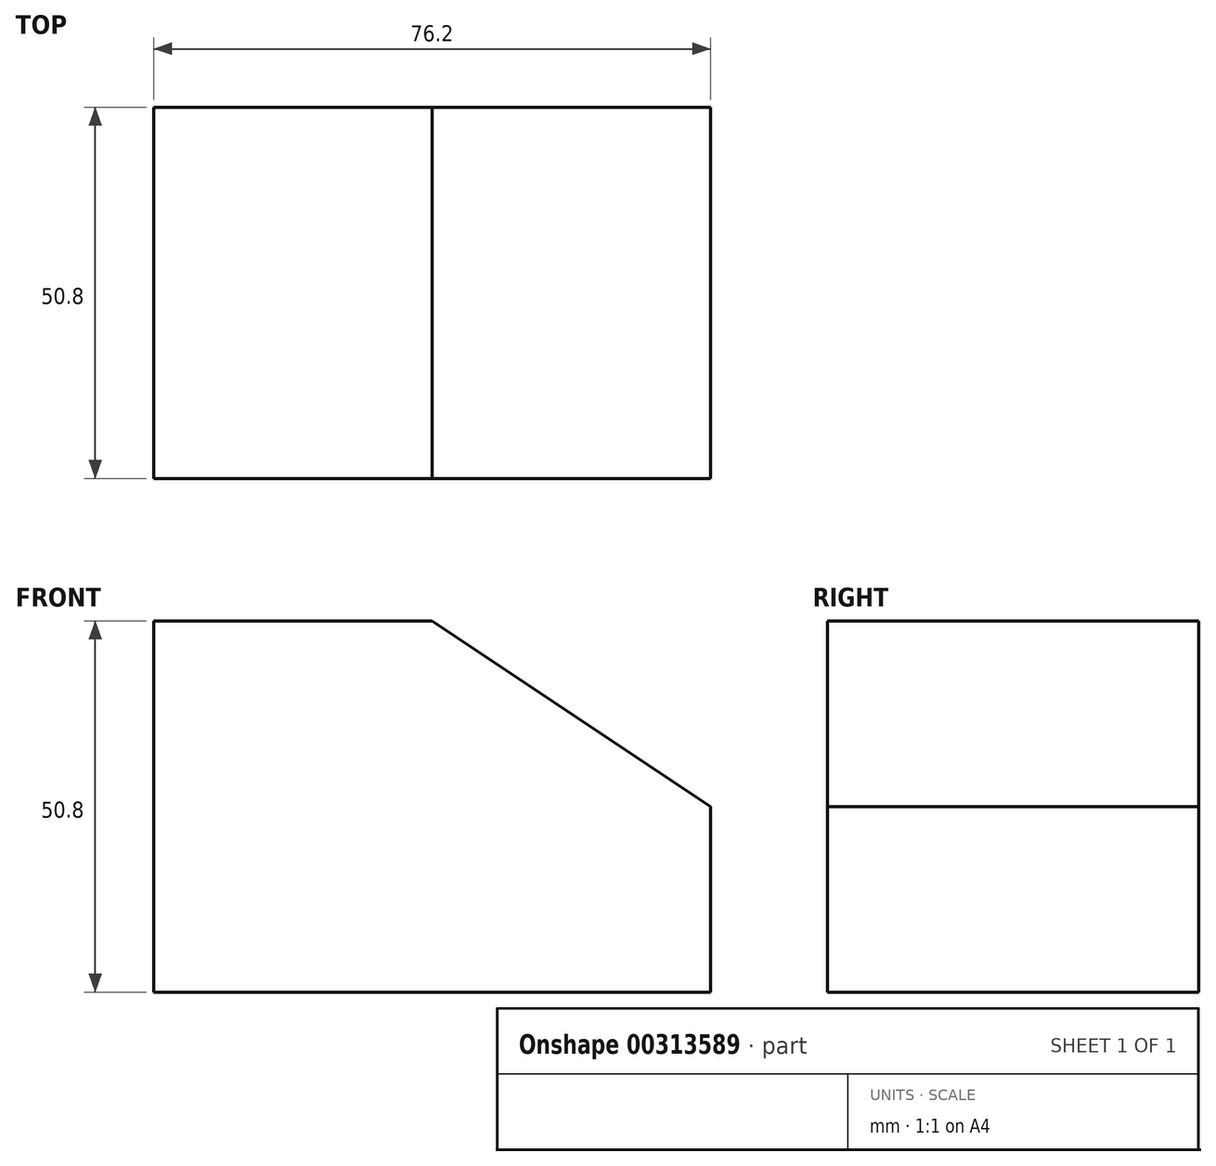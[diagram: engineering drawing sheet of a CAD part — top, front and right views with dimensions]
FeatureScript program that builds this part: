
annotation { "Feature Type Name" : "Feature", "Feature Type Description" : "" }
export const myFeature = defineFeature(function(context is Context, id is Id, definition is map)
    precondition{}
    {
        {
            var Q0;
            Q0=qCreatedBy(makeId("Front.planeOp"),FACE);
            var sketch = newSketch(context, id + "F0", { "sketchPlane" : qUnion([Q0])});
            skLineSegment(sketch, "E0", {"start": v(-33.68, -46.8) * mm, "end": v(42.52, -46.8) * mm});
            skLineSegment(sketch, "E1", {"start": v(42.52, -46.8) * mm, "end": v(42.52, -21.4) * mm});
            skLineSegment(sketch, "E2", {"start": v(-33.68, -46.8) * mm, "end": v(-33.68, 4) * mm});
            skLineSegment(sketch, "E3", {"start": v(-33.68, 4) * mm, "end": v(4.42, 4) * mm});
            skLineSegment(sketch, "E4", {"start": v(4.42, 4) * mm, "end": v(42.52, -21.4) * mm});
            skSolve(sketch);
        }
        {
            var Q0;
            Q0 = qSketchRegion(id + "F0", true);
            var Q1;
            Q1=makeQuery(id+"F0.imprint","IMPRINT",FACE,{"disambiguationData":[TD([[makeQuery(id+"F0.imprint","IMPRINT",EDGE,{"derivedFrom":sQuery(id+"F0.wireOp",EDGE,"E0")}),1.0]])]});
            extrude(context, id + "F1", {"entities" : qUnion([Q0, Q1]), "oppositeDirection" : true, "depth" : 50.8 * mm});
        }
    });
